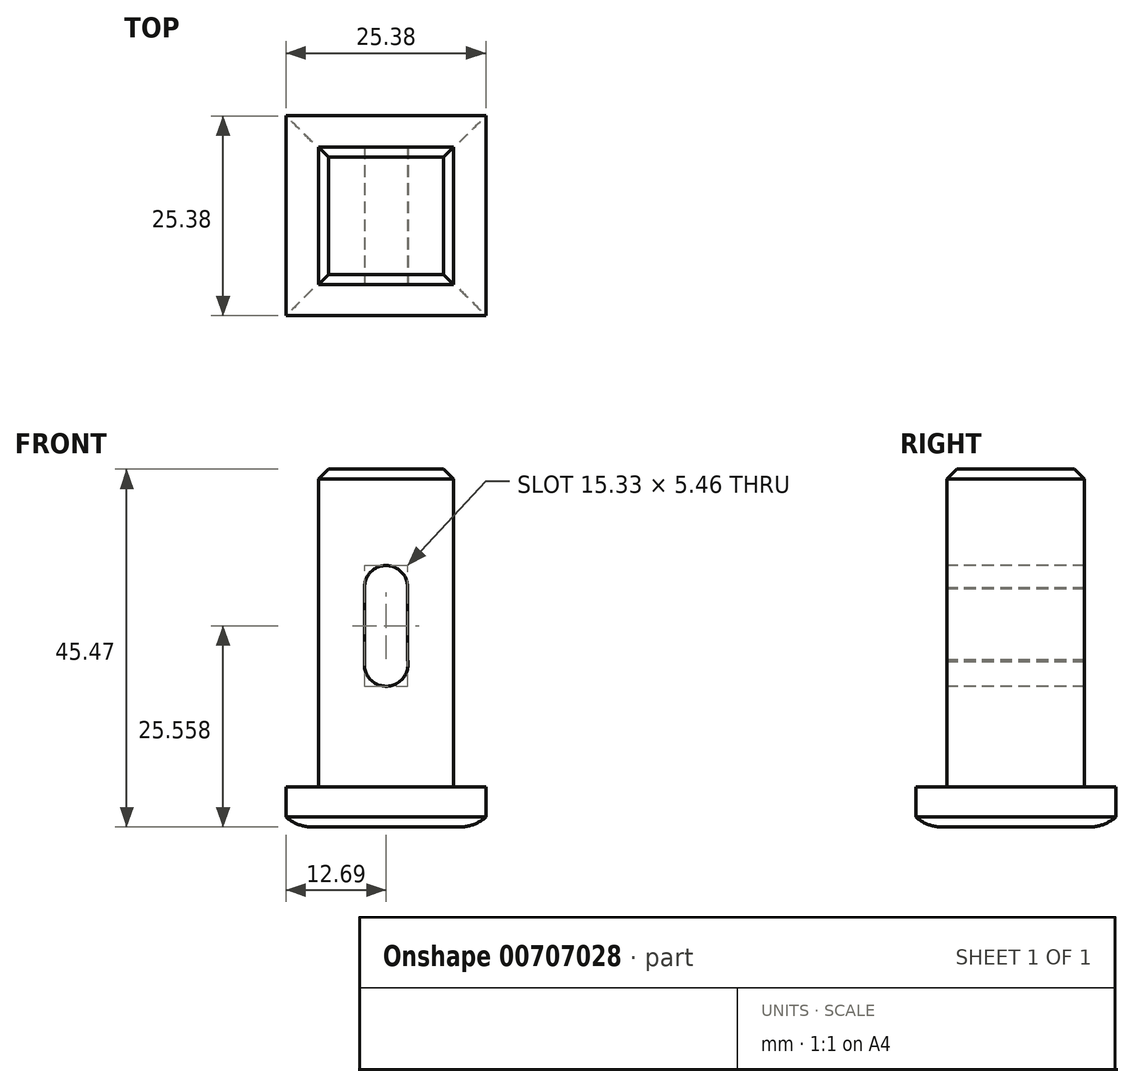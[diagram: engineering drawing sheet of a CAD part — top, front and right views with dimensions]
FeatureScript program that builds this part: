
annotation { "Feature Type Name" : "Feature", "Feature Type Description" : "" }
export const myFeature = defineFeature(function(context is Context, id is Id, definition is map)
    precondition{}
    {
        {
            var Q0;
            Q0=qCreatedBy(makeId("Top.planeOp"),FACE);
            var sketch = newSketch(context, id + "F0", { "sketchPlane" : qUnion([Q0])});
            skLineSegment(sketch, "E0.bottom", {"start": v(-12.7, -12.7) * mm, "end": v(12.7, -12.7) * mm});
            skLineSegment(sketch, "E0.top", {"start": v(-12.7, 12.7) * mm, "end": v(12.7, 12.7) * mm});
            skLineSegment(sketch, "E0.left", {"start": v(-12.7, -12.7) * mm, "end": v(-12.7, 12.7) * mm});
            skLineSegment(sketch, "E0.right", {"start": v(12.7, -12.7) * mm, "end": v(12.7, 12.7) * mm});
            skPoint(sketch, "E0.middle", {"position": v(0, 0) * mm});
            skSolve(sketch);
        }
        {
            var Q0;
            Q0 = qSketchRegion(id + "F0", true);
            extrude(context, id + "F1", {"entities" : qUnion([Q0]), "depth" : 5.08 * mm, "offsetDistance" : 25.4 * mm});
        }
        {
            var Q0;
            Q0=qCreatedBy(makeId("Top.planeOp"),FACE);
            var sketch = newSketch(context, id + "F2", { "sketchPlane" : qUnion([Q0])});
            skLineSegment(sketch, "E1.bottom", {"start": v(-8.55, 8.72) * mm, "end": v(8.55, 8.72) * mm});
            skLineSegment(sketch, "E1.top", {"start": v(-8.55, -8.72) * mm, "end": v(8.55, -8.72) * mm});
            skLineSegment(sketch, "E1.left", {"start": v(-8.55, 8.72) * mm, "end": v(-8.55, -8.72) * mm});
            skLineSegment(sketch, "E1.right", {"start": v(8.55, 8.72) * mm, "end": v(8.55, -8.72) * mm});
            skPoint(sketch, "E1.middle", {"position": v(0, 0) * mm});
            skSolve(sketch);
        }
        {
            var Q0;
            Q0 = qSketchRegion(id + "F2", true);
            extrude(context, id + "F3", {"entities" : qUnion([Q0]), "operationType" : NewBodyOperationType.ADD, "depth" : 45.47 * mm, "offsetDistance" : 25.4 * mm});
        }
        {
            var Q0;
            Q0=qCreatedBy(makeId("Front.planeOp"),FACE);
            var sketch = newSketch(context, id + "F4", { "sketchPlane" : qUnion([Q0])});
            skLineSegment(sketch, "E2.bottom", {"start": v(0, 17.89) * mm, "end": v(0.04, 17.89) * mm});
            skLineSegment(sketch, "E2.top", {"start": v(-0.98, 33.04) * mm, "end": v(1, 33.04) * mm});
            skLineSegment(sketch, "E2.left", {"start": v(-2.73, 20.35) * mm, "end": v(-2.73, 30.58) * mm});
            skLineSegment(sketch, "E2.right", {"start": v(2.73, 20.08) * mm, "end": v(2.73, 30.75) * mm});
            skPoint(sketch, "E2.middle", {"position": v(0, 25.47) * mm});
            skArc(sketch, "E3", {"start": v(2.73, 30.22) * mm, "mid": v(2.74, 30.49) * mm, "end": v(2.73, 30.75) * mm});
            skPoint(sketch, "E3.first.point", {"position": v(-2.73, 30.4) * mm});
            skPoint(sketch, "E3.second.point", {"position": v(2.73, 30.22) * mm});
            skPoint(sketch, "E3.third.point", {"position": v(2.73, 30.75) * mm});
            skArc(sketch, "E4", {"start": v(-2.73, 20.96) * mm, "mid": v(0.16, 17.9) * mm, "end": v(2.73, 21.24) * mm});
            skPoint(sketch, "E4.first.point", {"position": v(-2.73, 20.35) * mm});
            skPoint(sketch, "E4.second.point", {"position": v(2.73, 21.24) * mm});
            skPoint(sketch, "E4.third.point", {"position": v(0, 17.89) * mm});
            skPoint(sketch, "E5.orphan", {"position": v(2.73, 17.89) * mm});
            skPoint(sketch, "E6.orphan", {"position": v(-2.73, 17.89) * mm});
            skArc(sketch, "E7.trimOffspring", {"start": v(1, 33.04) * mm, "mid": v(-1.58, 32.72) * mm, "end": v(-2.73, 30.4) * mm});
            skPoint(sketch, "E8.orphan", {"position": v(-2.73, 33.04) * mm});
            skPoint(sketch, "E9.orphan", {"position": v(2.73, 33.04) * mm});
            skArc(sketch, "E10", {"start": v(2.73, 30.22) * mm, "mid": v(0.1, 33.23) * mm, "end": v(-2.73, 30.4) * mm});
            skSolve(sketch);
        }
        {
            var Q0;
            Q0 = qSketchRegion(id + "F4", true);
            extrude(context, id + "F5", {"entities" : qUnion([Q0]), "operationType" : NewBodyOperationType.REMOVE, "oppositeDirection" : true, "depth" : 25.4 * mm, "offsetDistance" : 25.4 * mm});
        }
        {
            var Q0;
            Q0=makeQuery(id+"F5.boolean.opBoolean","COPY",FACE,{"derivedFrom":makeQuery(id+"F5.opExtrude","CAP_FACE",FACE,{"disambiguationData":[OSD([sQuery(id+"F4.wireOp",EDGE,"E2.left"),sQuery(id+"F4.wireOp",EDGE,"E2.right"),sQuery(id+"F4.wireOp",EDGE,"E4"),sQuery(id+"F4.wireOp",EDGE,"E10")])],"isStart":true})});
            extrude(context, id + "F6", {"entities" : qUnion([Q0]), "operationType" : NewBodyOperationType.REMOVE, "oppositeDirection" : true, "depth" : 25.4 * mm, "offsetDistance" : 25.4 * mm});
        }
        {
            var Q0;
            Q0=makeQuery(id+"F1.opExtrude","CAP_EDGE",EDGE,{"disambiguationData":[OSD([sQuery(id+"F0.wireOp",EDGE,"E0.bottom")])],"isStart":true});
            var Q1;
            Q1=makeQuery(id+"F1.opExtrude","CAP_EDGE",EDGE,{"disambiguationData":[OSD([sQuery(id+"F0.wireOp",EDGE,"E0.right")])],"isStart":true});
            var Q2;
            Q2=makeQuery(id+"F1.opExtrude","CAP_EDGE",EDGE,{"disambiguationData":[OSD([sQuery(id+"F0.wireOp",EDGE,"E0.left")])],"isStart":true});
            var Q3;
            Q3=makeQuery(id+"F1.opExtrude","CAP_EDGE",EDGE,{"disambiguationData":[OSD([sQuery(id+"F0.wireOp",EDGE,"E0.top")])],"isStart":true});
            chamfer(context, id + "F7", {"entities" : qUnion([Q0, Q1, Q2, Q3]), "width" : 1.27 * mm, "tangentPropagation" : true});
        }
        {
            var Q0;
            Q0=makeQuery(id+"F3.opExtrude","CAP_FACE",FACE,{"disambiguationData":[OSD([sQuery(id+"F2.wireOp",EDGE,"E1.bottom"),sQuery(id+"F2.wireOp",EDGE,"E1.top"),sQuery(id+"F2.wireOp",EDGE,"E1.left"),sQuery(id+"F2.wireOp",EDGE,"E1.right")])],"isStart":false});
            chamfer(context, id + "F8", {"entities" : qUnion([Q0]), "width" : 1.27 * mm, "tangentPropagation" : true});
        }
        {
            var Q0;
            {var subQ0=sQuery(id+"F0.wireOp",EDGE,"E0.bottom");Q0=makeQuery(id+"F7.opChamfer","BLEND_EDGE",EDGE,{"blendedFrom":[makeQuery(id+"F1.opExtrude","CAP_EDGE",EDGE,{"disambiguationData":[OSD([subQ0])],"isStart":true}),makeQuery(id+"F1.opExtrude","CAP_FACE",FACE,{"disambiguationData":[OSD([subQ0,sQuery(id+"F0.wireOp",EDGE,"E0.top"),sQuery(id+"F0.wireOp",EDGE,"E0.left"),sQuery(id+"F0.wireOp",EDGE,"E0.right")])],"isStart":true})],"blendedInto":[makeQuery(id+"F1.opExtrude","CAP_FACE",FACE,{"disambiguationData":[OSD([subQ0,sQuery(id+"F0.wireOp",EDGE,"E0.top"),sQuery(id+"F0.wireOp",EDGE,"E0.left"),sQuery(id+"F0.wireOp",EDGE,"E0.right")])],"isStart":true})]});}
            var Q1;
            {var subQ0=sQuery(id+"F0.wireOp",EDGE,"E0.right");Q1=makeQuery(id+"F7.opChamfer","BLEND_EDGE",EDGE,{"blendedFrom":[makeQuery(id+"F1.opExtrude","CAP_EDGE",EDGE,{"disambiguationData":[OSD([subQ0])],"isStart":true}),makeQuery(id+"F1.opExtrude","CAP_FACE",FACE,{"disambiguationData":[OSD([sQuery(id+"F0.wireOp",EDGE,"E0.bottom"),sQuery(id+"F0.wireOp",EDGE,"E0.top"),sQuery(id+"F0.wireOp",EDGE,"E0.left"),subQ0])],"isStart":true})],"blendedInto":[makeQuery(id+"F1.opExtrude","CAP_FACE",FACE,{"disambiguationData":[OSD([sQuery(id+"F0.wireOp",EDGE,"E0.bottom"),sQuery(id+"F0.wireOp",EDGE,"E0.top"),sQuery(id+"F0.wireOp",EDGE,"E0.left"),subQ0])],"isStart":true})]});}
            var Q2;
            {var subQ0=sQuery(id+"F0.wireOp",EDGE,"E0.top");Q2=makeQuery(id+"F7.opChamfer","BLEND_EDGE",EDGE,{"blendedFrom":[makeQuery(id+"F1.opExtrude","CAP_EDGE",EDGE,{"disambiguationData":[OSD([subQ0])],"isStart":true}),makeQuery(id+"F1.opExtrude","CAP_FACE",FACE,{"disambiguationData":[OSD([sQuery(id+"F0.wireOp",EDGE,"E0.bottom"),subQ0,sQuery(id+"F0.wireOp",EDGE,"E0.left"),sQuery(id+"F0.wireOp",EDGE,"E0.right")])],"isStart":true})],"blendedInto":[makeQuery(id+"F1.opExtrude","CAP_FACE",FACE,{"disambiguationData":[OSD([sQuery(id+"F0.wireOp",EDGE,"E0.bottom"),subQ0,sQuery(id+"F0.wireOp",EDGE,"E0.left"),sQuery(id+"F0.wireOp",EDGE,"E0.right")])],"isStart":true})]});}
            var Q3;
            {var subQ0=sQuery(id+"F0.wireOp",EDGE,"E0.left");Q3=makeQuery(id+"F7.opChamfer","BLEND_EDGE",EDGE,{"blendedFrom":[makeQuery(id+"F1.opExtrude","CAP_EDGE",EDGE,{"disambiguationData":[OSD([subQ0])],"isStart":true}),makeQuery(id+"F1.opExtrude","CAP_FACE",FACE,{"disambiguationData":[OSD([sQuery(id+"F0.wireOp",EDGE,"E0.bottom"),sQuery(id+"F0.wireOp",EDGE,"E0.top"),subQ0,sQuery(id+"F0.wireOp",EDGE,"E0.right")])],"isStart":true})],"blendedInto":[makeQuery(id+"F1.opExtrude","CAP_FACE",FACE,{"disambiguationData":[OSD([sQuery(id+"F0.wireOp",EDGE,"E0.bottom"),sQuery(id+"F0.wireOp",EDGE,"E0.top"),subQ0,sQuery(id+"F0.wireOp",EDGE,"E0.right")])],"isStart":true})]});}
            fillet(context, id + "F9", {"entities" : qUnion([Q0, Q1, Q2, Q3]), "tangentPropagation" : true, "radius" : 5.08 * mm, "defaultsChanged" : false, "vertexSettings" : [], "allowEdgeOverflow" : false});
        }
    });
